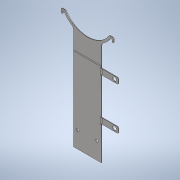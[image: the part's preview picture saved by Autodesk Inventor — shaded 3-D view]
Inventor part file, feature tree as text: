
AUTODESK INVENTOR PART (.ipt)
format: ipt  version: 2020.3 (Build 243373000, 373)  size: 343,552 bytes
history: native  units: mm
features: sheet_metal_op x9, sketch x7, chamfer x5, other x4, hole x2, extrude x1, fillet x1
ambient origin geometry x8: Origin, YZ Plane, XZ Plane, XY Plane, X Axis, Y Axis, Z Axis, Center Point
bodies: Solid1 (feature_tree)
feature tree (29):
  sheet_metal_op  "Face1"
  sheet_metal_op  "Flange1"
  sheet_metal_op  "Face2"
  chamfer  "Corner Round7"
  extrude  "Extrusion1"  Depth=50.0mm
  sketch  "Sketch5"  dims[d7=79.0mm d8=90.0deg d9=1.0mm]
  hole  "Hole1"  [1 undecoded]
  chamfer  "Corner Round12"
  chamfer  "Corner Round13"
  chamfer  "Corner Round14"
  chamfer  "Corner Round15"
  sheet_metal_op  "Face4"
  hole  "Hole2"  [1 undecoded]
  fillet  "Fillet1"  Radius=1.0mm
  sheet_metal_op  "Unfold1"
  sketch  "Sketch1"  dims[d0=50.0mm d1=150.0mm]
  other  "Plate1"
  sketch  "Sketch2"  dims[d2=1.0mm d3=1.0mm]
  other  "Plate2"
  sheet_metal_op  "Bend1"
  sheet_metal_op  "Corner1"
  sketch  "Sketch4"  dims[d4=0.5mm d5=2.0mm d6=1.0mm]
  other  "Plate3"
  sheet_metal_op  "Bend2"
  sketch  "Sketch7"  dims[d10=4.0mm]
  sketch  "Sketch13"  dims[d11=1.0mm]
  other  "Plate5"
  sheet_metal_op  "Bend4"
  sketch  "Sketch14"  dims[d12=1.0mm d13=91.0mm d14=40.0mm d15=40.0mm d16=40.0mm d17=40.0mm d18=1.0mm d19=1.0mm d20=0.5mm d21=2.0mm d22=1.0mm d23=0.0mm d24=0.0mm d30=9.0mm d31=109.0mm d37=30.0mm d38=8.0mm d39=8.0mm d40=4.5mm d41=4.5mm d42=4.0mm d43=2.0mm d44=90.0deg d45=1.0mm d46=20.594885mm d61=6.0mm d84=22.0mm d85=8.0mm d86=0.0mm d87=8.0mm d88=3.0mm d89=8.0mm d90=180.0deg d91=8.0mm d92=90.0deg d93=3.0mm d95=5.0mm d96=5.0mm d97=2.0mm d98=1.5mm d99=1.5mm d100=1.0mm d101=2.0mm d102=1.5mm d103=1.0mm d104=1.0mm d105=1.0mm d106=3.0mm d107=3.0mm d109=92.6mm d115=1.3mm d116=1.3mm d117=45.792087mm d118=6.839208mm d119=1.3mm d120=1.3mm d121=45.792087mm d133=30.0mm d134=10.0mm d135=146.0mm d136=30.0mm d137=10.0mm d138=66.0mm d139=1.0mm d140=1.0mm d141=0.5mm d142=2.0mm d143=1.0mm d144=23.0mm d145=5.0mm d146=5.0mm d147=7.0mm d148=6.0mm d149=4.0mm d150=2.0mm d151=90.0deg d152=1.0mm d153=20.594885mm d154=76.0mm d155=2.0mm]
note: 2 required parameter values undecoded (feature->parameter linkage not recoverable at this tier; creation-order binding heuristic only, values carry confidence <= 0.55)
